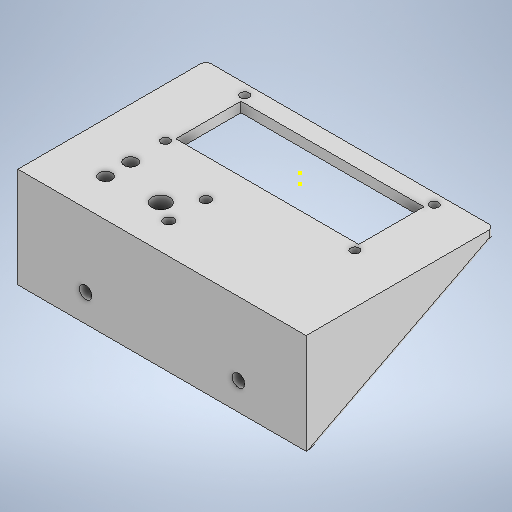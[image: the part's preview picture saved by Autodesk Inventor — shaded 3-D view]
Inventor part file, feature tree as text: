
AUTODESK INVENTOR PART (.ipt)
format: ipt  version: 2025.2 (Build 292293000, 293)  size: 451,584 bytes
history: native  units: mm
features: sketch x17, extrude x12, fillet x5, hole x3, mirror x2, other x1
ambient origin geometry x8: Origin, YZ Plane, XZ Plane, XY Plane, X Axis, Y Axis, Z Axis, Center Point
bodies: Body1 (feature_tree)
feature tree (40):
  other  "Bryła1"
  extrude  "Wyciągnięcie proste1"  Depth=85.0mm
  hole  "Otwór1"  [1 undecoded]
  extrude  "Wyciągnięcie proste2"  Depth=4.0mm TaperAngle=0.0deg
  extrude  "Wyciągnięcie proste3"  Depth=75.6mm
  extrude  "Wyciągnięcie proste4"  Depth=31.6mm
  sketch  "Szkic6"
  extrude  "Wyciągnięcie proste5"  Depth=73.0mm
  mirror  "Odbij1"
  extrude  "Wyciągnięcie proste6"  Depth=26.0mm
  extrude  "Wyciągnięcie proste7"  TaperAngle=0.0deg  [1 undecoded]
  extrude  "Wyciągnięcie proste8"  Depth=85.0mm
  mirror  "Odbij2"
  fillet  "Zaokrąglenie1"  Radius=30.0mm
  fillet  "Zaokrąglenie2"  Radius=4.0mm
  fillet  "Zaokrąglenie3"  Radius=100.0mm
  fillet  "Zaokrąglenie4"  Radius=40.0mm
  extrude  "Wyciągnięcie proste9"  Depth=5.0mm TaperAngle=0.0deg
  fillet  "Zaokrąglenie5"  Radius=15.0mm
  extrude  "Wyciągnięcie proste10"  Depth=75.0mm
  extrude  "Wyciągnięcie proste11"  Depth=4.0mm TaperAngle=0.0deg
  hole  "Otwór2"  [1 undecoded]
  hole  "Otwór3"  [1 undecoded]
  extrude  "Wyciągnięcie proste12"  Depth=10.0mm
  sketch  "Szkic19"
  sketch  "Szkic1"
  sketch  "Szkic2"
  sketch  "Szkic3"
  sketch  "Szkic4"
  sketch  "Szkic5"
  sketch  "Szkic7"
  sketch  "Szkic8"
  sketch  "Szkic9"
  sketch  "Szkic10"
  sketch  "Szkic12"
  sketch  "Szkic13"
  sketch  "Szkic15"
  sketch  "Szkic16"
  sketch  "Szkic17"
  sketch  "Szkic18"
note: 4 required parameter values undecoded (feature->parameter linkage not recoverable at this tier; creation-order binding heuristic only, values carry confidence <= 0.55)
